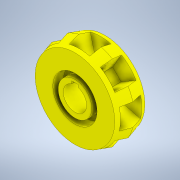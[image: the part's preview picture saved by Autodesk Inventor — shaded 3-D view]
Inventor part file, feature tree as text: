
AUTODESK INVENTOR PART (.ipt)
format: ipt  version: 2020.2 (Build 242310000, 310)  size: 209,408 bytes
history: native  units: mm
features: sketch x6, extrude x4, mirror x1, revolve x1, pattern_circular x1
ambient origin geometry x8: Origin, YZ Plane, XZ Plane, XY Plane, X Axis, Y Axis, Z Axis, Center Point
bodies: Solid1 (feature_tree)
feature tree (13):
  extrude  "Extrusion1"  Depth=17.0mm TaperAngle=0.0deg
  extrude  "Extrusion2"  Depth=3.5mm
  extrude  "Extrusion3"  TaperAngle=0.0deg  [1 undecoded]
  mirror  "Mirror1"
  revolve  "Revolution1"  [1 undecoded]
  extrude  "Extrusion4"  Depth=2.5mm
  pattern_circular  "Circular Pattern1"  [2 undecoded]
  sketch  "Sketch6"  dims[d13=90.0deg d14=13.0mm d15=12.0mm d16=12.0mm d17=0.0mm d18=80.0mm d19=360.0deg d21=41.0mm]
  sketch  "Sketch1"  dims[d0=45.0mm d1=17.0mm d2=0.0mm]
  sketch  "Sketch2"  dims[d3=13.2mm d4=3.5mm]
  sketch  "Sketch3"  dims[d5=1.5mm d6=0.0mm d7=0.0mm]
  sketch  "Sketch4"  dims[d8=19.0mm d9=3.0mm]
  sketch  "Sketch5"  dims[d10=6.0mm d11=0.0mm d12=2.5mm]
note: 4 required parameter values undecoded (feature->parameter linkage not recoverable at this tier; creation-order binding heuristic only, values carry confidence <= 0.55)